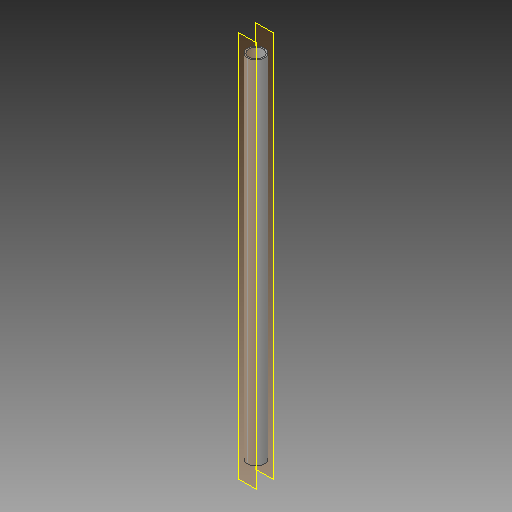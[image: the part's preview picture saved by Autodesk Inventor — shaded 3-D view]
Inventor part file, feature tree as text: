
AUTODESK INVENTOR PART (.ipt)
format: ipt  version: 2018 (Build 220112000, 112)  size: 87,040 bytes
history: native  units: mm
features: other x2, extrude x1, sketch x1
ambient origin geometry x8: Origin, YZ Plane, XZ Plane, XY Plane, X Axis, Y Axis, Z Axis, Center Point
bodies: Solid1 (feature_tree)
feature tree (4):
  extrude  "Extrusion1"  Depth=1000.0mm
  other  "rørtangent 1"
  other  "rørtangent 2"
  sketch  "Sketch1"  dims[d0=48.5mm d1=3.75mm d2=41.0mm d3=1000.0mm d4=0.0mm]
